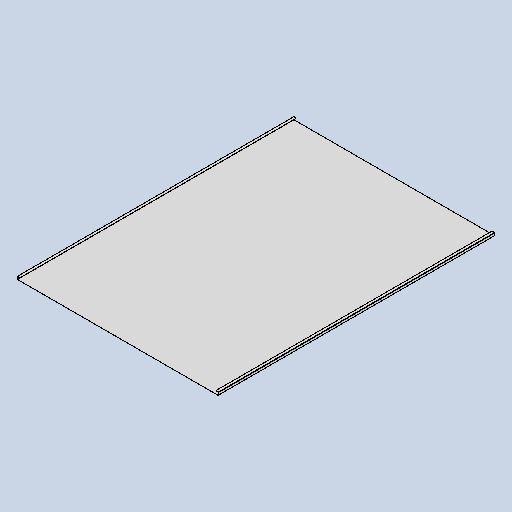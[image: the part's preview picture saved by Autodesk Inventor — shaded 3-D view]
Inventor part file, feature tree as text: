
AUTODESK INVENTOR PART (.ipt)
format: ipt  version: 2025 (Build 290162010, 162A)  size: 201,216 bytes
history: native  units: mm
features: sheet_metal_op x13, other x6, sketch x5, chamfer x1
ambient origin geometry x8: Origin, YZ Plane, XZ Plane, XY Plane, X Axis, Y Axis, Z Axis, Center Point
bodies: Body1 (feature_tree)
feature tree (25):
  sheet_metal_op  "Face1"
  sheet_metal_op  "Flange2"
  sheet_metal_op  "Flange3"
  sheet_metal_op  "Flange4"
  sheet_metal_op  "Flange5"
  chamfer  "Corner Round1"
  sketch  "Sketch6"  dims[d12=23.212879mm]
  other  "Plate2"
  sketch  "Sketch11"  dims[d52=713.4mm]
  other  "Plate4"
  sheet_metal_op  "Bend3"
  sheet_metal_op  "Corner3"
  sketch  "Sketch12"  dims[d53=980.0mm]
  other  "Plate5"
  sheet_metal_op  "Bend4"
  sheet_metal_op  "Corner4"
  sketch  "Sketch13"  dims[d54=0.5mm]
  other  "Plate6"
  sheet_metal_op  "Bend5"
  sheet_metal_op  "Corner5"
  sketch  "Sketch14"  dims[d84=0.5mm d85=0.25mm d86=1.0mm d87=0.5mm d88=10.0mm d89=90.0deg d90=0.5mm d91=2.0mm d92=0.5mm d93=0.5mm d94=0.5mm d95=0.25mm d96=1.0mm d97=0.5mm d98=10.0mm d99=90.0deg d100=0.5mm d101=2.0mm d102=0.5mm d103=0.5mm d104=0.5mm d105=0.25mm d106=1.0mm d107=0.5mm d108=10.0mm d109=90.0deg d110=0.5mm d111=2.0mm d112=0.5mm d113=0.5mm d114=0.5mm d115=0.25mm d116=1.0mm d117=0.5mm d118=10.0mm d119=90.0deg d120=0.5mm d121=2.0mm d122=0.5mm d123=0.5mm d124=4.0mm]
  other  "Plate7"
  sheet_metal_op  "Bend6"
  sheet_metal_op  "Corner6"
  other  "Definition1"
